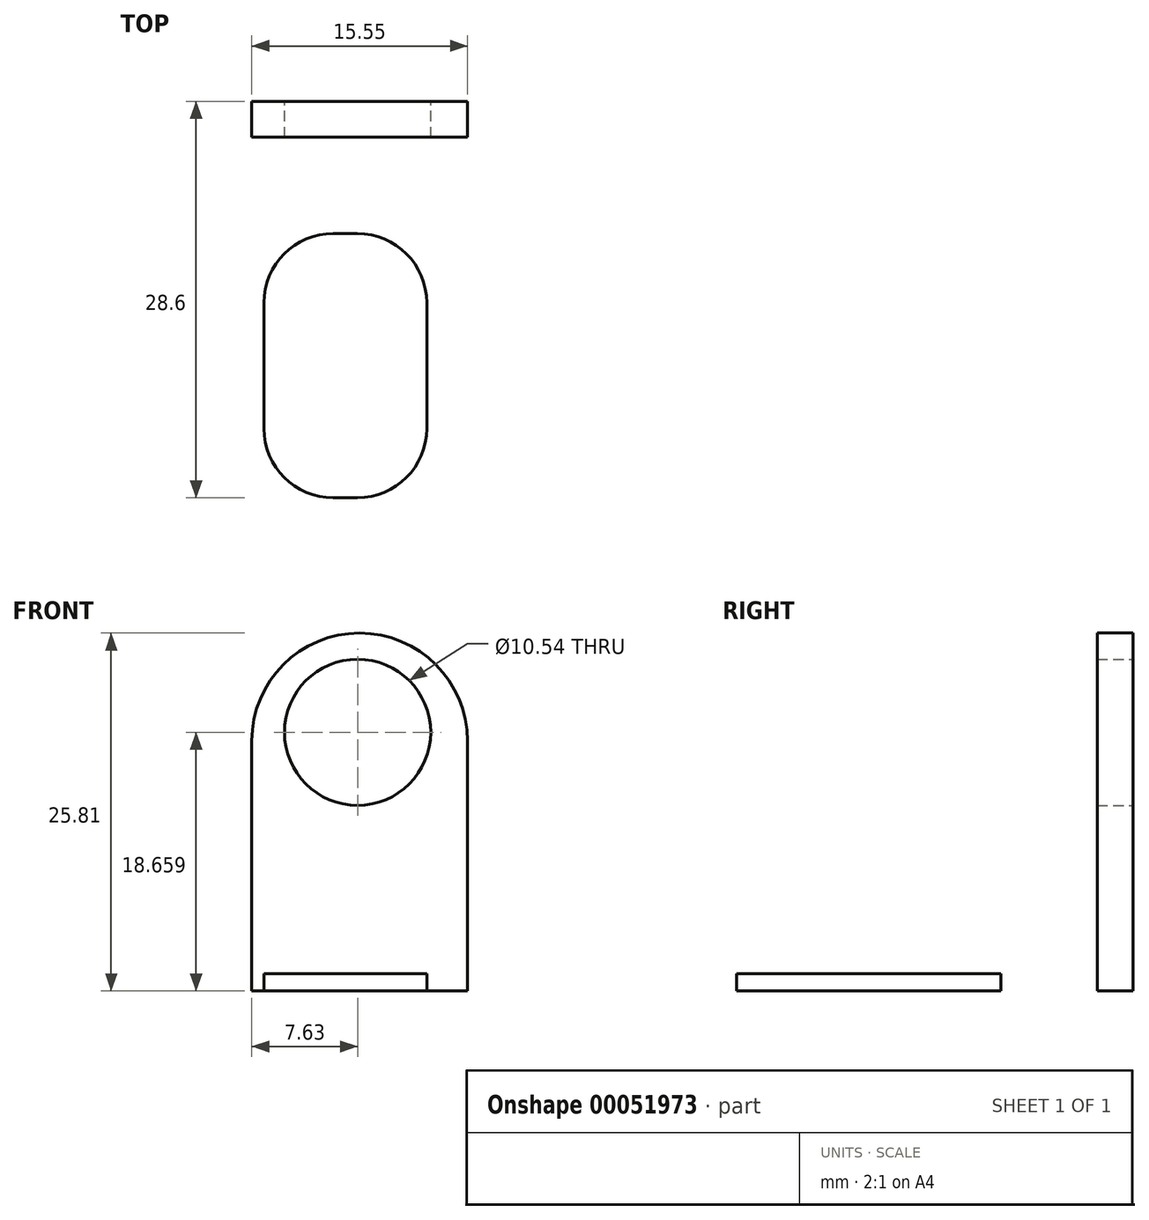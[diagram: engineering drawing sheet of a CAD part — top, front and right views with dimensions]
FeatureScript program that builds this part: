
annotation { "Feature Type Name" : "Feature", "Feature Type Description" : "" }
export const myFeature = defineFeature(function(context is Context, id is Id, definition is map)
    precondition{}
    {
        {
            var Q0;
            Q0=qCreatedBy(makeId("Front.planeOp"),FACE);
            var sketch = newSketch(context, id + "F0", { "sketchPlane" : qUnion([Q0])});
            skLineSegment(sketch, "E0", {"start": v(-45.17, 0) * mm, "end": v(-45.17, 18.04) * mm});
            skLineSegment(sketch, "E1", {"start": v(-29.62, 0) * mm, "end": v(-29.62, 18.04) * mm});
            skArc(sketch, "E2", {"start": v(-29.62, 18.04) * mm, "mid": v(-37.4, 25.81) * mm, "end": v(-45.17, 18.04) * mm});
            skLineSegment(sketch, "E3", {"start": v(-45.17, 0) * mm, "end": v(-29.62, 0) * mm});
            skSolve(sketch);
        }
        {
            var Q0;
            Q0 = qSketchRegion(id + "F0", true);
            extrude(context, id + "F1", {"entities" : qUnion([Q0]), "depth" : 2.6 * mm});
        }
        {
            var Q0;
            Q0=qCreatedBy(makeId("Front.planeOp"),FACE);
            var sketch = newSketch(context, id + "F2", { "sketchPlane" : qUnion([Q0])});
            skCircle(sketch, "E4", {"center": v(-37.54, 18.66) * mm, "radius": 5.27 * mm});
            skSolve(sketch);
        }
        {
            var Q0;
            Q0 = qSketchRegion(id + "F2", true);
            extrude(context, id + "F3", {"entities" : qUnion([Q0]), "operationType" : NewBodyOperationType.REMOVE, "depth" : 25 * mm});
        }
        {
            var Q0;
            Q0=qCreatedBy(makeId("Top.planeOp"),FACE);
            var sketch = newSketch(context, id + "F4", { "sketchPlane" : qUnion([Q0])});
            skLineSegment(sketch, "E5.bottom", {"start": v(-44.29, -9.53) * mm, "end": v(-32.56, -9.53) * mm});
            skLineSegment(sketch, "E5.top", {"start": v(-44.29, -28.6) * mm, "end": v(-32.56, -28.6) * mm});
            skLineSegment(sketch, "E5.left", {"start": v(-44.29, -9.53) * mm, "end": v(-44.29, -28.6) * mm});
            skLineSegment(sketch, "E5.right", {"start": v(-32.56, -9.53) * mm, "end": v(-32.56, -28.6) * mm});
            skSolve(sketch);
        }
        {
            var Q0;
            Q0 = qSketchRegion(id + "F4", true);
            extrude(context, id + "F5", {"entities" : qUnion([Q0]), "depth" : 1.24 * mm});
        }
        {
            var Q0;
            Q0=makeQuery(id+"F5.opExtrude","SWEPT_EDGE",EDGE,{"disambiguationData":[OSD([sQuery(id+"F4.wireOp",EDGE,"E5.bottom"),sQuery(id+"F4.wireOp",EDGE,"E5.right")])]});
            var Q1;
            Q1=makeQuery(id+"F5.opExtrude","SWEPT_EDGE",EDGE,{"disambiguationData":[OSD([sQuery(id+"F4.wireOp",EDGE,"E5.bottom"),sQuery(id+"F4.wireOp",EDGE,"E5.left")])]});
            var Q2;
            Q2=makeQuery(id+"F5.opExtrude","SWEPT_EDGE",EDGE,{"disambiguationData":[OSD([sQuery(id+"F4.wireOp",EDGE,"E5.top"),sQuery(id+"F4.wireOp",EDGE,"E5.right")])]});
            var Q3;
            Q3=makeQuery(id+"F5.opExtrude","SWEPT_EDGE",EDGE,{"disambiguationData":[OSD([sQuery(id+"F4.wireOp",EDGE,"E5.top"),sQuery(id+"F4.wireOp",EDGE,"E5.left")])]});
            fillet(context, id + "F6", {"entities" : qUnion([Q0, Q1, Q2, Q3]), "radius" : 5 * mm, "tangentPropagation" : true, "allowEdgeOverflow" : false});
        }
    });
